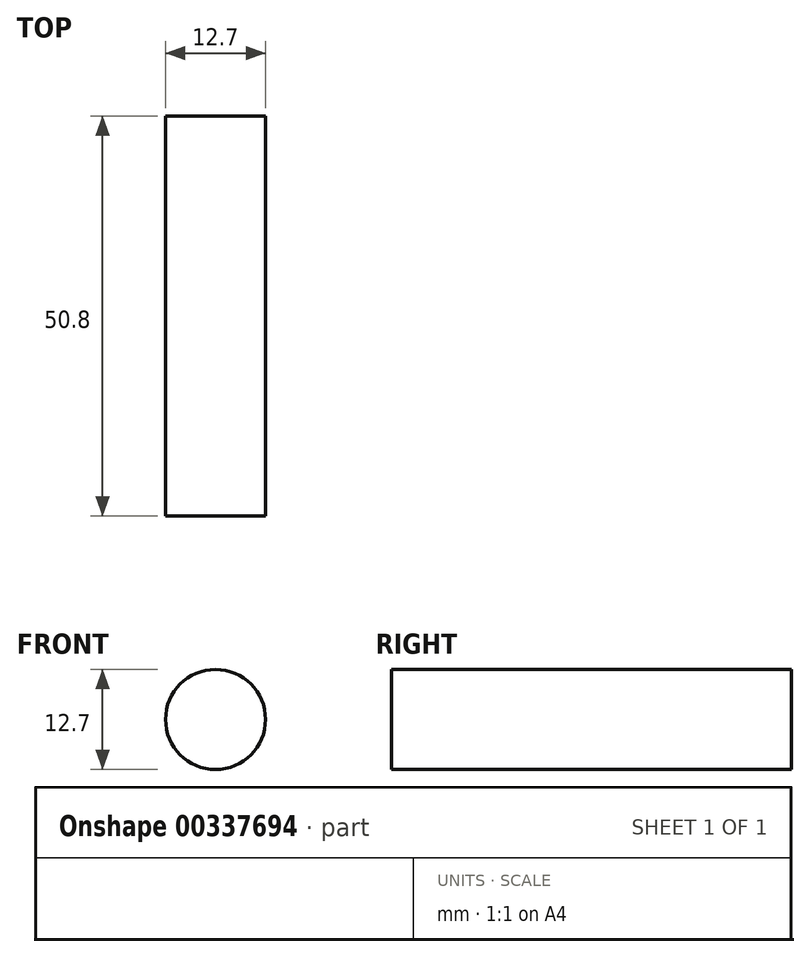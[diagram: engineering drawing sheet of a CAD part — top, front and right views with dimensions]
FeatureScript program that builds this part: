
annotation { "Feature Type Name" : "Feature", "Feature Type Description" : "" }
export const myFeature = defineFeature(function(context is Context, id is Id, definition is map)
    precondition{}
    {
        {
            var Q0;
            Q0=qCreatedBy(makeId("Front.planeOp"),FACE);
            var sketch = newSketch(context, id + "F0", { "sketchPlane" : qUnion([Q0])});
            skCircle(sketch, "E0", {"center": v(0, 0) * mm, "radius": 6.35 * mm});
            skSolve(sketch);
        }
        {
            var Q0;
            Q0 = qSketchRegion(id + "F0", true);
            extrude(context, id + "F1", {"entities" : qUnion([Q0]), "depth" : 50.8 * mm});
        }
    });
